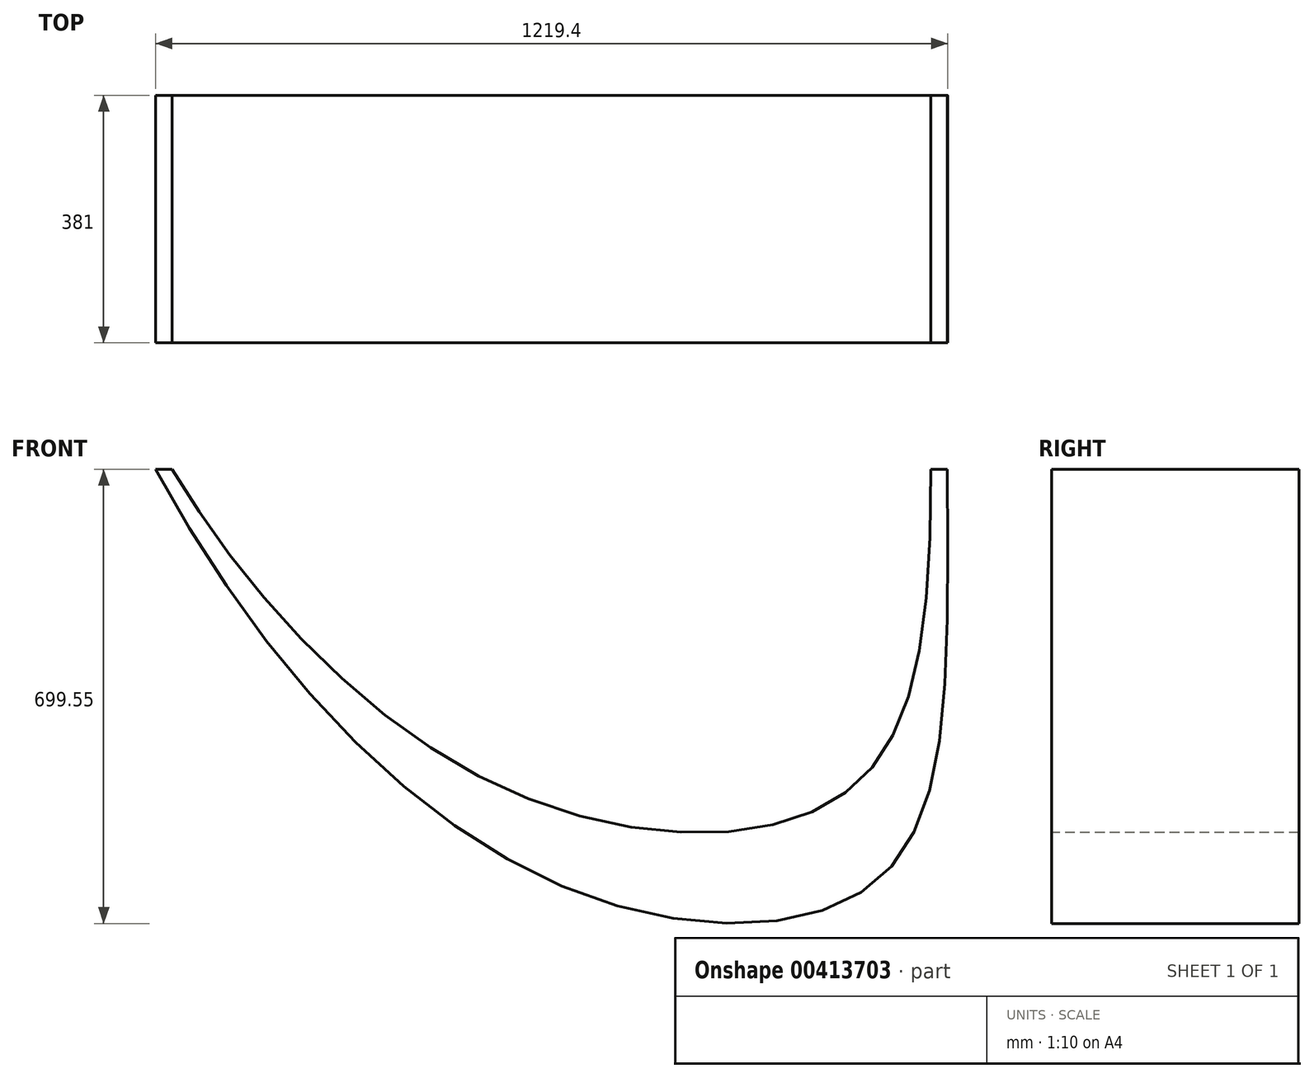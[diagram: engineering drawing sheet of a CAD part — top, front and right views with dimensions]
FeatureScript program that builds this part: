
annotation { "Feature Type Name" : "Feature", "Feature Type Description" : "" }
export const myFeature = defineFeature(function(context is Context, id is Id, definition is map)
    precondition{}
    {
        {
            var Q0;
            Q0=qCreatedBy(makeId("Front.planeOp"),FACE);
            var sketch = newSketch(context, id + "F0", { "sketchPlane" : qUnion([Q0])});
            skLineSegment(sketch, "E0.bottom", {"start": v(0, 0) * mm, "end": v(1219.2, 0) * mm, "construction": true});
            skLineSegment(sketch, "E0.top", {"start": v(0, 635) * mm, "end": v(1219.2, 635) * mm, "construction": true});
            skLineSegment(sketch, "E0.left", {"start": v(0, 0) * mm, "end": v(0, 635) * mm, "construction": true});
            skLineSegment(sketch, "E0.right", {"start": v(1219.2, 0) * mm, "end": v(1219.2, 635) * mm, "construction": true});
            skFitSpline(sketch, "E1", {"points": [v(0, 635) * mm, v(609.6, 0) * mm, v(1109.27, 0) * mm, v(1219.2, 635) * mm], "startDerivative": vector(1127.7, -2107.14) * mm, "endDerivative": vector(0, 2904.42) * mm});
            skLineSegment(sketch, "E2", {"start": v(25.4, 635) * mm, "end": v(25.4, 0) * mm, "construction": true});
            skLineSegment(sketch, "E3", {"start": v(1193.8, 635) * mm, "end": v(1193.8, 0) * mm, "construction": true});
            skFitSpline(sketch, "E4", {"points": [v(25.4, 635) * mm, v(530.94, 145.95) * mm, v(1046.38, 126.32) * mm, v(1193.8, 635) * mm], "startDerivative": vector(888.53, -1493.15) * mm, "endDerivative": vector(0, 2550.27) * mm});
            skLineSegment(sketch, "E5", {"start": v(0, 635) * mm, "end": v(25.4, 635) * mm});
            skLineSegment(sketch, "E6", {"start": v(1193.8, 635) * mm, "end": v(1219.2, 635) * mm});
            skPoint(sketch, "E7", {"position": v(1058.36, -32) * mm});
            skPoint(sketch, "E8", {"position": v(1058.36, 635) * mm});
            skLineSegment(sketch, "E9", {"start": v(871.59, 635) * mm, "end": v(871.59, -64.14) * mm, "construction": true});
            skSolve(sketch);
        }
        {
            var Q0;
            Q0 = qSketchRegion(id + "F0", true);
            extrude(context, id + "F1", {"entities" : qUnion([Q0]), "endBound" : BoundingType.SYMMETRIC, "depth" : 381 * mm});
        }
    });
